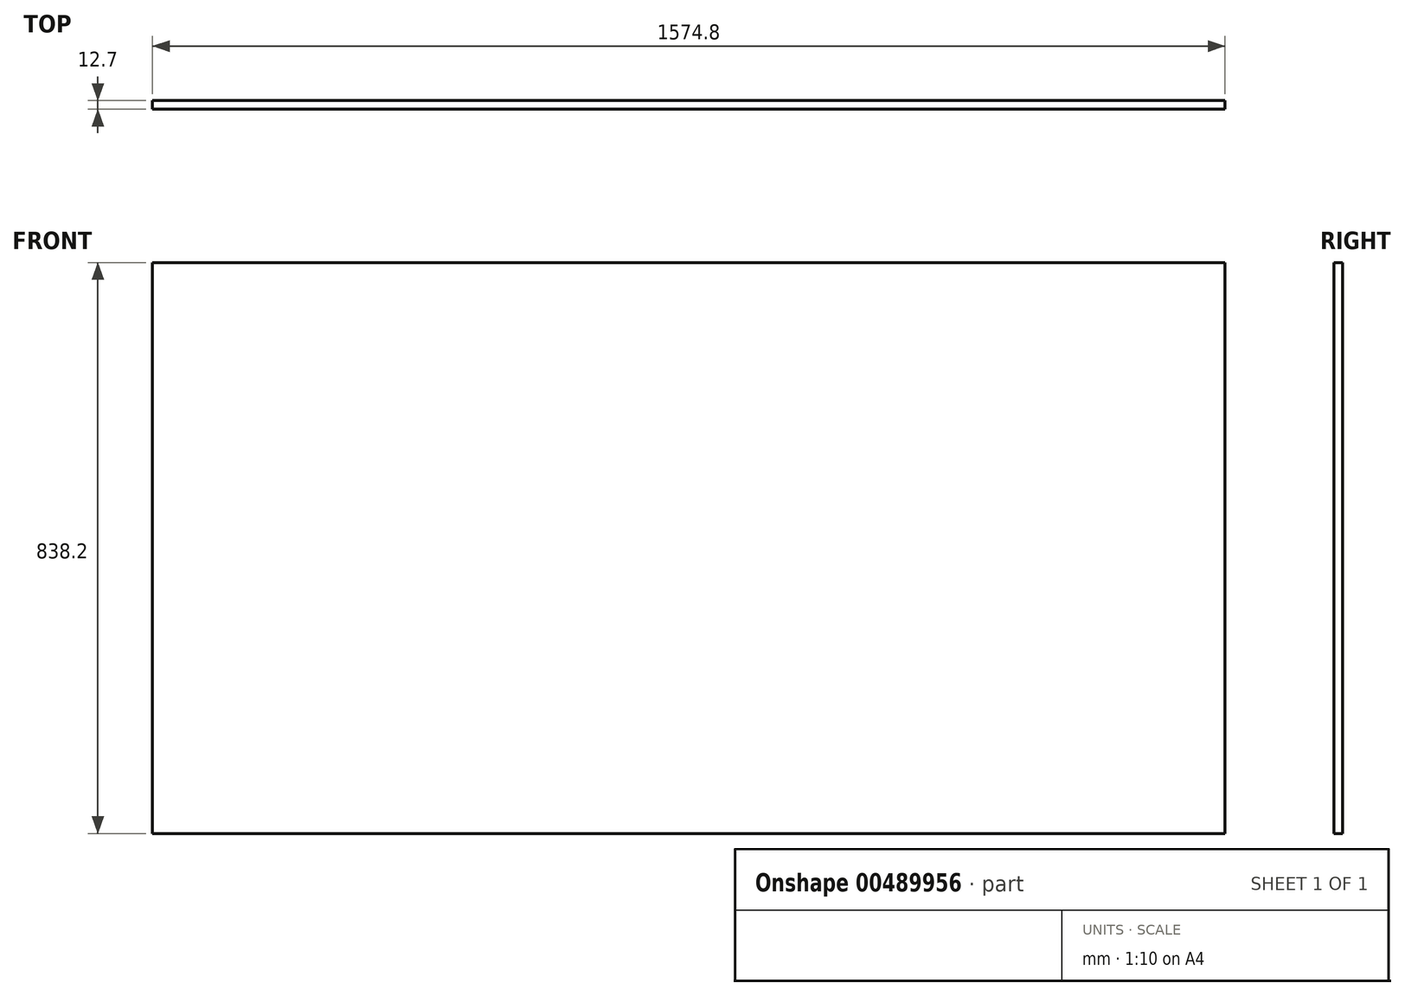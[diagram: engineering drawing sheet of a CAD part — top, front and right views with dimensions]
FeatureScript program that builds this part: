
annotation { "Feature Type Name" : "Feature", "Feature Type Description" : "" }
export const myFeature = defineFeature(function(context is Context, id is Id, definition is map)
    precondition{}
    {
        {
            var Q0;
            Q0=qCreatedBy(makeId("Front.planeOp"),FACE);
            var sketch = newSketch(context, id + "F0", { "sketchPlane" : qUnion([Q0])});
            skLineSegment(sketch, "E0.bottom", {"start": v(-787.4, 419.1) * mm, "end": v(787.4, 419.1) * mm});
            skLineSegment(sketch, "E0.top", {"start": v(-787.4, -419.1) * mm, "end": v(787.4, -419.1) * mm});
            skLineSegment(sketch, "E0.left", {"start": v(-787.4, 419.1) * mm, "end": v(-787.4, -419.1) * mm});
            skLineSegment(sketch, "E0.right", {"start": v(787.4, 419.1) * mm, "end": v(787.4, -419.1) * mm});
            skPoint(sketch, "E0.middle", {"position": v(0, 0) * mm});
            skSolve(sketch);
        }
        {
            var Q0;
            Q0 = qSketchRegion(id + "F0", true);
            extrude(context, id + "F1", {"entities" : qUnion([Q0]), "depth" : 12.7 * mm});
        }
    });
